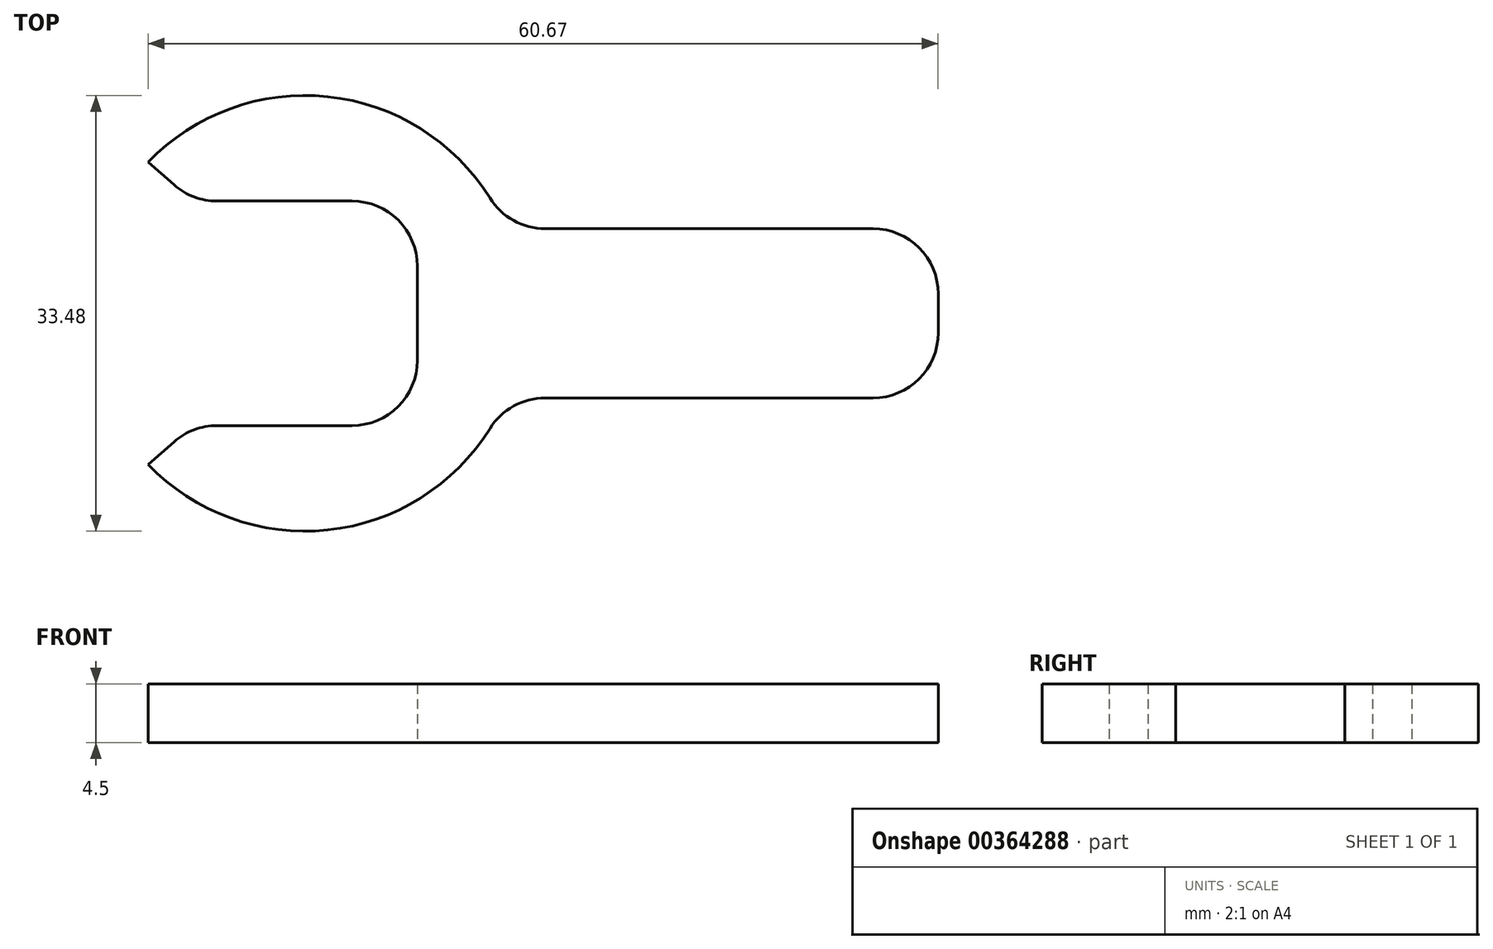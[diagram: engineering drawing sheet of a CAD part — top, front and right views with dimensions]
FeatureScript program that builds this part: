
annotation { "Feature Type Name" : "Feature", "Feature Type Description" : "" }
export const myFeature = defineFeature(function(context is Context, id is Id, definition is map)
    precondition{}
    {
        {
            var Q0;
            Q0=qCreatedBy(makeId("Top.planeOp"),FACE);
            var sketch = newSketch(context, id + "F0", { "sketchPlane" : qUnion([Q0])});
            skLineSegment(sketch, "E0.bottom", {"start": v(3.63, 8.62) * mm, "end": v(-6.75, 8.62) * mm});
            skLineSegment(sketch, "E0.top", {"start": v(3.63, -8.62) * mm, "end": v(-6.75, -8.62) * mm});
            skLineSegment(sketch, "E0.left", {"start": v(8.62, 3.63) * mm, "end": v(8.62, -3.63) * mm});
            skPoint(sketch, "E0.middle", {"position": v(0, 0) * mm});
            skArc(sketch, "E1", {"start": v(-12.05, -11.62) * mm, "mid": v(1.75, -16.65) * mm, "end": v(14.2, -8.85) * mm});
            skLineSegment(sketch, "E2", {"start": v(-10.04, 9.86) * mm, "end": v(-12.05, 11.62) * mm});
            skLineSegment(sketch, "E3.bottom", {"start": v(18.45, 6.5) * mm, "end": v(43.63, 6.5) * mm});
            skLineSegment(sketch, "E3.top", {"start": v(18.45, -6.5) * mm, "end": v(43.63, -6.5) * mm});
            skLineSegment(sketch, "E3.right", {"start": v(48.62, 1.5) * mm, "end": v(48.62, -1.5) * mm});
            skPoint(sketch, "E3.middle", {"position": v(31.96, 0) * mm});
            skLineSegment(sketch, "E4.MirrorCS", {"start": v(-10.04, -9.86) * mm, "end": v(-12.05, -11.62) * mm});
            skArc(sketch, "E5.trimOffspring", {"start": v(14.2, 8.85) * mm, "mid": v(1.75, 16.65) * mm, "end": v(-12.05, 11.62) * mm});
            skPoint(sketch, "E6.orphan", {"position": v(15.3, 6.5) * mm});
            skPoint(sketch, "E7.orphan", {"position": v(15.3, -6.5) * mm});
            skPoint(sketch, "E8.visualSharp", {"position": v(48.63, 6.5) * mm});
            skArc(sketch, "E8.filletArc", {"start": v(48.62, 1.5) * mm, "mid": v(47.16, 5.04) * mm, "end": v(43.63, 6.5) * mm});
            skPoint(sketch, "E9.visualSharp", {"position": v(48.63, -6.5) * mm});
            skArc(sketch, "E9.filletArc", {"start": v(43.63, -6.5) * mm, "mid": v(47.16, -5.04) * mm, "end": v(48.62, -1.5) * mm});
            skPoint(sketch, "E10.visualSharp", {"position": v(15.43, -6.5) * mm});
            skArc(sketch, "E10.filletArc", {"start": v(18.45, -6.5) * mm, "mid": v(16.02, -7.13) * mm, "end": v(14.2, -8.85) * mm});
            skPoint(sketch, "E11.visualSharp", {"position": v(15.43, 6.5) * mm});
            skArc(sketch, "E11.filletArc", {"start": v(14.2, 8.85) * mm, "mid": v(16.02, 7.13) * mm, "end": v(18.45, 6.5) * mm});
            skPoint(sketch, "E12.visualSharp", {"position": v(-8.63, 8.62) * mm});
            skArc(sketch, "E12.filletArc", {"start": v(-10.04, 9.86) * mm, "mid": v(-8.5, 8.94) * mm, "end": v(-6.75, 8.62) * mm});
            skPoint(sketch, "E13.visualSharp", {"position": v(-8.63, -8.62) * mm});
            skArc(sketch, "E13.filletArc", {"start": v(-6.75, -8.62) * mm, "mid": v(-8.5, -8.94) * mm, "end": v(-10.04, -9.86) * mm});
            skPoint(sketch, "E14.visualSharp", {"position": v(8.62, 8.62) * mm});
            skArc(sketch, "E14.filletArc", {"start": v(8.62, 3.63) * mm, "mid": v(7.16, 7.16) * mm, "end": v(3.63, 8.62) * mm});
            skPoint(sketch, "E15.visualSharp", {"position": v(8.62, -8.62) * mm});
            skArc(sketch, "E15.filletArc", {"start": v(3.63, -8.62) * mm, "mid": v(7.16, -7.16) * mm, "end": v(8.62, -3.63) * mm});
            skSolve(sketch);
        }
        {
            var Q0;
            Q0 = qSketchRegion(id + "F0", true);
            extrude(context, id + "F1", {"entities" : qUnion([Q0]), "depth" : 4.5 * mm});
        }
    });
